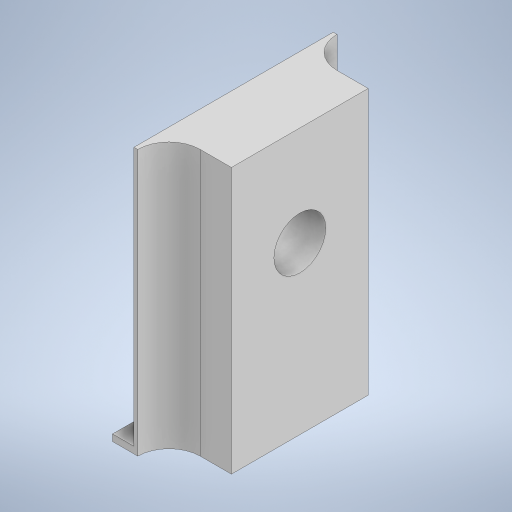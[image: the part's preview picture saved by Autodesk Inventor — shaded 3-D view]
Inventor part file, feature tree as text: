
AUTODESK INVENTOR PART (.ipt)
format: ipt  version: 2023 (Build 270158000, 158)  size: 240,128 bytes
history: native  units: in
note: dims shown in document units (in); Inventor stores cm internally (conversion verified against a paired STEP export)
features: extrude x3, sketch x2
ambient origin geometry x8: Origin, YZ Plane, XZ Plane, XY Plane, X Axis, Y Axis, Z Axis, Center Point
bodies: Solid1 (feature_tree)
feature tree (5):
  sketch  "Sketch1"  dims[d2=0.094in d3=0.094in]
  extrude  "Extrusion1"  Depth=0.094in
  extrude  "Extrusion3"  Depth=0.01in
  extrude  "Extrusion4"  Depth=0.01in
  sketch  "Sketch2"  dims[d4=0.4in d5=0.0in d8=0.0781in d9=0.25in d10=5.0in d11=0.0in d12=0.132in d13=0.01in d14=0.0in]
